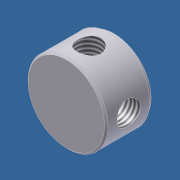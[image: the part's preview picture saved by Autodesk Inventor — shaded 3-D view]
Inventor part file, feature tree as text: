
AUTODESK INVENTOR PART (.ipt)
format: ipt  version: unknown  size: 218,112 bytes
history: native  units: in
note: dims shown in document units (in); Inventor stores cm internally (conversion verified against a paired STEP export)
features: sketch x5, extrude x4, thread x4, plane x3, chamfer x1, projected_geometry x1
ambient origin geometry x8: Origin, YZ Plane, XZ Plane, XY Plane, X Axis, Y Axis, Z Axis, Center Point
bodies: Solid1 (feature_tree)
feature tree (18):
  extrude  "Extrusion1"  Depth=0.775in TaperAngle=0.0deg
  chamfer  "Chamfer1"  Distance=0.0312in Angle=45.0deg
  extrude  "Extrusion2"  Depth=0.075in TaperAngle=0.0deg
  plane  "Work Plane1"
  extrude  "Extrusion3"  Depth=0.425in
  plane  "Work Plane2"
  sketch  "Sketch4"  dims[d11=3.0in d12=0.0in d13=0.0in d14=0.0in d15=0.425in d16=3.0in d17=0.0in d18=1.0in d19=0.0in]
  plane  "Work Plane3"
  extrude  "Extrusion4"  TaperAngle=0.0deg  [1 undecoded]
  thread  "Thread1"  [1 undecoded]
  thread  "Thread2"  [1 undecoded]
  thread  "Thread3"  [1 undecoded]
  thread  "Thread4"  [1 undecoded]
  sketch  "Sketch1"  dims[d0=1.425in d1=0.775in d2=0.0in d3=0.0312in d4=0.125in d5=45.0deg]
  sketch  "Sketch2"  dims[d6=1.325in d7=0.075in d8=0.0in]
  sketch  "Sketch3"  dims[d9=0.0in d10=0.425in]
  projected_geometry  "Projected Loop1"
  sketch  "Sketch5"  dims[d20=1.0in d21=0.0in d22=1.0in d23=0.0in d24=1.0in d25=0.0in]
note: 5 required parameter values undecoded (feature->parameter linkage not recoverable at this tier; creation-order binding heuristic only, values carry confidence <= 0.55)
